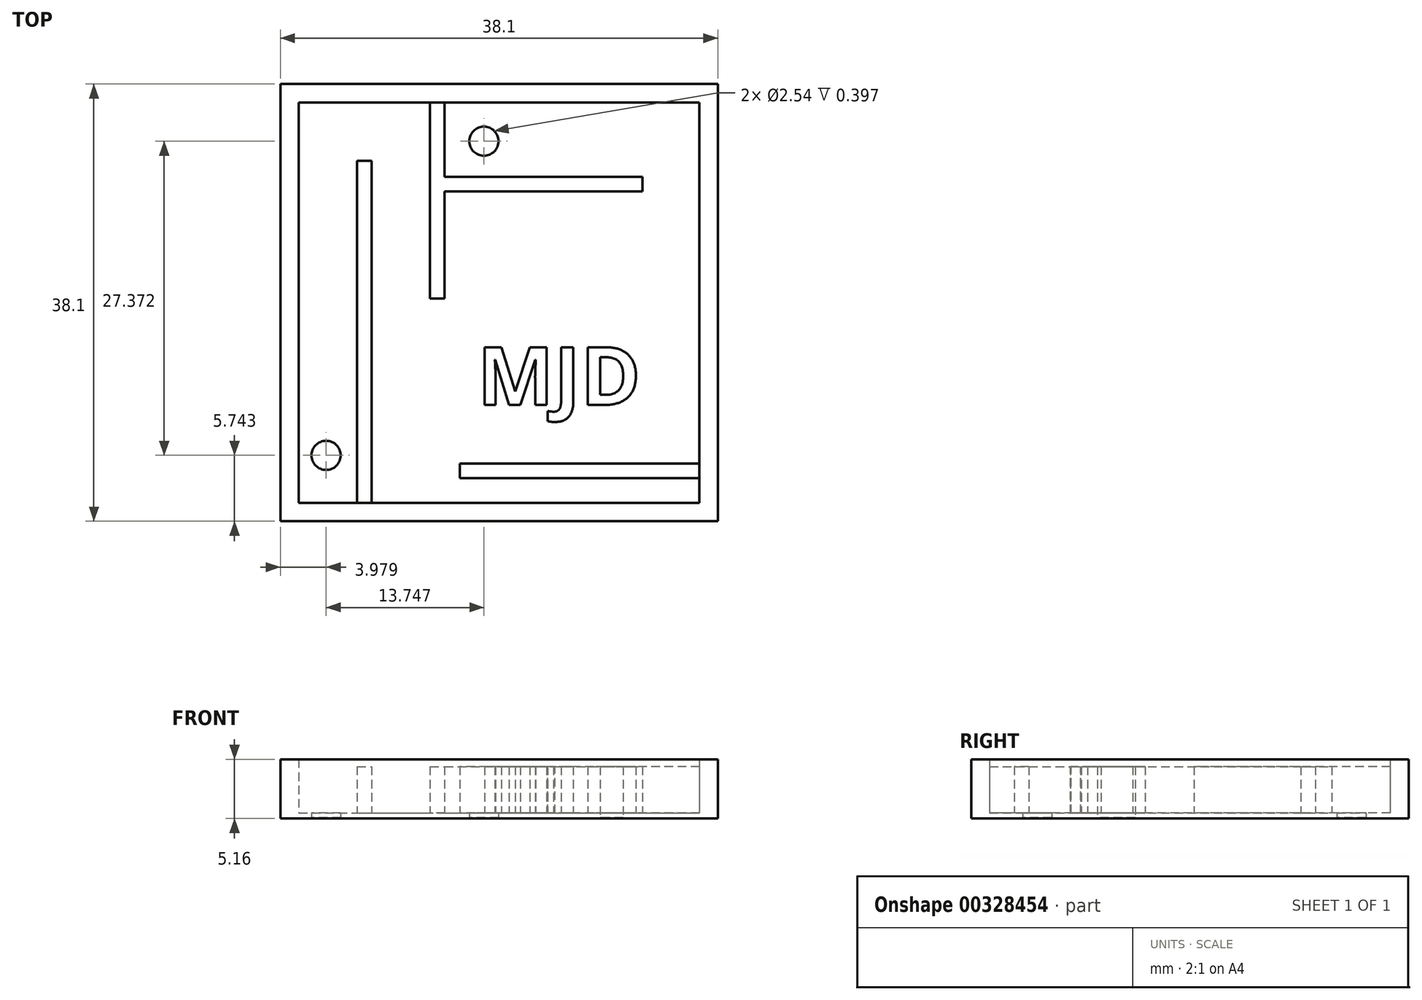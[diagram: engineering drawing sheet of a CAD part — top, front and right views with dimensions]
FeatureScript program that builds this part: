
annotation { "Feature Type Name" : "Feature", "Feature Type Description" : "" }
export const myFeature = defineFeature(function(context is Context, id is Id, definition is map)
    precondition{}
    {
        {
            var Q0;
            Q0=qCreatedBy(makeId("Top.planeOp"),FACE);
            var sketch = newSketch(context, id + "F0", { "sketchPlane" : qUnion([Q0])});
            skLineSegment(sketch, "E0.bottom", {"start": v(-22.73, 22.17) * mm, "end": v(15.37, 22.17) * mm});
            skLineSegment(sketch, "E0.top", {"start": v(-22.73, -15.93) * mm, "end": v(15.37, -15.93) * mm});
            skLineSegment(sketch, "E0.left", {"start": v(-22.73, 22.17) * mm, "end": v(-22.73, -15.93) * mm});
            skLineSegment(sketch, "E0.right", {"start": v(15.37, 22.17) * mm, "end": v(15.37, -15.93) * mm});
            skSolve(sketch);
        }
        {
            var Q0;
            Q0=makeQuery(id+"F0.imprint","IMPRINT",FACE,{"disambiguationData":[TD([[makeQuery(id+"F0.imprint","IMPRINT",EDGE,{"derivedFrom":sQuery(id+"F0.wireOp",EDGE,"E0.bottom")}),-1.0]])]});
            extrude(context, id + "F1", {"entities" : qUnion([Q0]), "depth" : 0.08 * mm});
        }
        {
            var Q0;
            Q0=makeQuery(id+"F1.opExtrude","CAP_FACE",FACE,{"disambiguationData":[OSD([sQuery(id+"F0.wireOp",EDGE,"E0.bottom"),sQuery(id+"F0.wireOp",EDGE,"E0.top"),sQuery(id+"F0.wireOp",EDGE,"E0.left"),sQuery(id+"F0.wireOp",EDGE,"E0.right")])],"isStart":false});
            var sketch = newSketch(context, id + "F2", { "sketchPlane" : qUnion([Q0])});
            skLineSegment(sketch, "E1.0", {"start": v(-21.13, 20.57) * mm, "end": v(13.77, 20.57) * mm});
            skLineSegment(sketch, "E1.1", {"start": v(-21.13, 20.57) * mm, "end": v(-21.13, -14.33) * mm});
            skLineSegment(sketch, "E1.2", {"start": v(-21.13, -14.33) * mm, "end": v(13.77, -14.33) * mm});
            skLineSegment(sketch, "E1.3", {"start": v(13.77, 20.57) * mm, "end": v(13.77, -14.33) * mm});
            skSolve(sketch);
        }
        {
            var Q0;
            Q0=makeQuery(id+"F2.imprint","IMPRINT",FACE,{"disambiguationData":[TD([[makeQuery(id+"F2.imprint","IMPRINT",EDGE,{"derivedFrom":sQuery(id+"F2.wireOp",EDGE,"E1.0")}),1.0]])]});
            extrude(context, id + "F3", {"entities" : qUnion([Q0]), "operationType" : NewBodyOperationType.ADD, "depth" : 5.08 * mm});
        }
        {
            var Q0;
            Q0=makeQuery(id+"F1.opExtrude","CAP_FACE",FACE,{"disambiguationData":[OSD([sQuery(id+"F0.wireOp",EDGE,"E0.bottom"),sQuery(id+"F0.wireOp",EDGE,"E0.top"),sQuery(id+"F0.wireOp",EDGE,"E0.left"),sQuery(id+"F0.wireOp",EDGE,"E0.right")])],"isStart":false});
            var sketch = newSketch(context, id + "F4", { "sketchPlane" : qUnion([Q0])});
            skLineSegment(sketch, "E2.bottom", {"start": v(-16.05, -14.33) * mm, "end": v(-14.78, -14.33) * mm});
            skLineSegment(sketch, "E2.top", {"start": v(-16.05, 15.49) * mm, "end": v(-14.78, 15.49) * mm});
            skLineSegment(sketch, "E2.left", {"start": v(-16.05, -14.33) * mm, "end": v(-16.05, 15.49) * mm});
            skLineSegment(sketch, "E2.right", {"start": v(-14.78, -14.33) * mm, "end": v(-14.78, 15.49) * mm});
            skLineSegment(sketch, "E3.bottom", {"start": v(-11.92, 20.57) * mm, "end": v(-9.7, 20.57) * mm});
            skLineSegment(sketch, "E4.bottom", {"start": v(13.77, -10.89) * mm, "end": v(-7.1, -10.89) * mm});
            skLineSegment(sketch, "E4.top", {"start": v(13.77, -12.16) * mm, "end": v(-7.1, -12.16) * mm});
            skLineSegment(sketch, "E4.left", {"start": v(13.77, -10.89) * mm, "end": v(13.77, -12.16) * mm});
            skLineSegment(sketch, "E4.right", {"start": v(-7.1, -10.89) * mm, "end": v(-7.1, -12.16) * mm});
            skText(sketch, "E5", { "text": "MJD", "fontName": "OpenSans-Bold.ttf"});
            skLineSegment(sketch, "E6.bottom", {"start": v(-8.43, 20.57) * mm, "end": v(-9.7, 20.57) * mm});
            skLineSegment(sketch, "E6.top", {"start": v(-8.43, 3.47) * mm, "end": v(-9.7, 3.47) * mm});
            skLineSegment(sketch, "E6.left", {"start": v(-8.43, 20.57) * mm, "end": v(-8.43, 14.07) * mm});
            skLineSegment(sketch, "E6.right", {"start": v(-9.7, 20.57) * mm, "end": v(-9.7, 3.47) * mm});
            skLineSegment(sketch, "E7.bottom", {"start": v(-8.43, 12.8) * mm, "end": v(8.8, 12.8) * mm});
            skLineSegment(sketch, "E7.top", {"start": v(-8.43, 14.07) * mm, "end": v(8.8, 14.07) * mm});
            skLineSegment(sketch, "E7.right", {"start": v(8.8, 12.8) * mm, "end": v(8.8, 14.07) * mm});
            skLineSegment(sketch, "E8.trimOffspring", {"start": v(-8.43, 12.8) * mm, "end": v(-8.43, 3.47) * mm});
            const initialGuessF4  = {"E5": [-0.00557, -0.0058, 1, 0, 0.00508]};
            skSetInitialGuess(sketch, initialGuessF4);
            skSolve(sketch);
        }
        {
            var Q0;
            Q0=makeQuery(id+"F4.imprint","IMPRINT",FACE,{"disambiguationData":[TD([[makeQuery(id+"F4.imprint","IMPRINT",EDGE,{"derivedFrom":sQuery(id+"F4.wireOp",EDGE,"E2.bottom")}),1.0]])]});
            var Q1;
            Q1=makeQuery(id+"F4.imprint","IMPRINT",FACE,{"disambiguationData":[TD([[makeQuery(id+"F4.imprint","IMPRINT",EDGE,{"derivedFrom":sQuery(id+"F4.wireOp",EDGE,"E6.bottom")}),-1.0]])]});
            var Q2;
            Q2=makeQuery(id+"F4.imprint","IMPRINT",FACE,{"disambiguationData":[TD([[makeQuery(id+"F4.imprint","IMPRINT",EDGE,{"derivedFrom":sQuery(id+"F4.wireOp",EDGE,"E4.bottom")}),1.0]])]});
            extrude(context, id + "F5", {"entities" : qUnion([Q0, Q1, Q2]), "operationType" : NewBodyOperationType.ADD, "depth" : 4.44 * mm});
        }
        {
            var Q0;
            Q0 = qSketchRegion(id + "F4", true);
            extrude(context, id + "F6", {"entities" : qUnion([Q0]), "operationType" : NewBodyOperationType.ADD, "depth" : 4.44 * mm});
        }
        {
            var Q0;
            Q0=makeQuery(id+"F4.imprint","IMPRINT",FACE,{"disambiguationData":[TD([[makeQuery(id+"F4.imprint","IMPRINT",EDGE,{"derivedFrom":sQuery(id+"F4.wireOp",EDGE,"E2.top")}),1.0]])]});
            var sketch = newSketch(context, id + "F7", { "sketchPlane" : qUnion([Q0])});
            skCircle(sketch, "E9", {"center": v(-5, 17.19) * mm, "radius": 1.27 * mm});
            skCircle(sketch, "E10", {"center": v(-18.75, -10.19) * mm, "radius": 1.27 * mm});
            skSolve(sketch);
        }
        {
            var Q0;
            Q0=makeQuery(id+"F7.imprint","IMPRINT",FACE,{"disambiguationData":[TD([[makeQuery(id+"F7.imprint","IMPRINT",EDGE,{"derivedFrom":sQuery(id+"F7.wireOp",EDGE,"E9")}),-1.0]])]});
            extrude(context, id + "F8", {"entities" : qUnion([Q0]), "operationType" : NewBodyOperationType.ADD, "depth" : 0.8 * mm});
        }
        {
            var Q0;
            Q0=makeQuery(id+"F8.opExtrude","CAP_FACE",FACE,{"disambiguationData":[OSD([sQuery(id+"F2.wireOp",EDGE,"E1.0"),sQuery(id+"F2.wireOp",EDGE,"E1.1"),sQuery(id+"F2.wireOp",EDGE,"E1.2"),sQuery(id+"F2.wireOp",EDGE,"E1.3"),sQuery(id+"F4.wireOp",EDGE,"E2.top"),sQuery(id+"F4.wireOp",EDGE,"E2.left"),sQuery(id+"F4.wireOp",EDGE,"E2.right"),sQuery(id+"F4.wireOp",EDGE,"E3.bottom"),sQuery(id+"F4.wireOp",EDGE,"E4.bottom"),sQuery(id+"F4.wireOp",EDGE,"E4.top"),sQuery(id+"F4.wireOp",EDGE,"E4.right"),sQuery(id+"F4.wireOp",EDGE,"E5.sketch_text.stroke-0"),sQuery(id+"F4.wireOp",EDGE,"E5.sketch_text.stroke-1"),sQuery(id+"F4.wireOp",EDGE,"E5.sketch_text.stroke-2"),sQuery(id+"F4.wireOp",EDGE,"E5.sketch_text.stroke-3"),sQuery(id+"F4.wireOp",EDGE,"E5.sketch_text.stroke-4"),sQuery(id+"F4.wireOp",EDGE,"E5.sketch_text.stroke-5"),sQuery(id+"F4.wireOp",EDGE,"E5.sketch_text.stroke-6"),sQuery(id+"F4.wireOp",EDGE,"E5.sketch_text.stroke-7"),sQuery(id+"F4.wireOp",EDGE,"E5.sketch_text.stroke-8"),sQuery(id+"F4.wireOp",EDGE,"E5.sketch_text.stroke-9"),sQuery(id+"F4.wireOp",EDGE,"E5.sketch_text.stroke-10"),sQuery(id+"F4.wireOp",EDGE,"E5.sketch_text.stroke-11"),sQuery(id+"F4.wireOp",EDGE,"E5.sketch_text.stroke-12"),sQuery(id+"F4.wireOp",EDGE,"E5.sketch_text.stroke-13"),sQuery(id+"F4.wireOp",EDGE,"E5.sketch_text.stroke-14"),sQuery(id+"F4.wireOp",EDGE,"E5.sketch_text.stroke-15"),sQuery(id+"F4.wireOp",EDGE,"E5.sketch_text.stroke-16"),sQuery(id+"F4.wireOp",EDGE,"E5.sketch_text.stroke-17"),sQuery(id+"F4.wireOp",EDGE,"E5.sketch_text.stroke-18"),sQuery(id+"F4.wireOp",EDGE,"E5.sketch_text.stroke-19"),sQuery(id+"F4.wireOp",EDGE,"E5.sketch_text.stroke-20"),sQuery(id+"F4.wireOp",EDGE,"E5.sketch_text.stroke-21"),sQuery(id+"F4.wireOp",EDGE,"E5.sketch_text.stroke-22"),sQuery(id+"F4.wireOp",EDGE,"E5.sketch_text.stroke-23"),sQuery(id+"F4.wireOp",EDGE,"E5.sketch_text.stroke-24"),sQuery(id+"F4.wireOp",EDGE,"E5.sketch_text.stroke-25"),sQuery(id+"F4.wireOp",EDGE,"E5.sketch_text.stroke-26"),sQuery(id+"F4.wireOp",EDGE,"E5.sketch_text.stroke-27"),sQuery(id+"F4.wireOp",EDGE,"E5.sketch_text.stroke-28"),sQuery(id+"F4.wireOp",EDGE,"E5.sketch_text.stroke-29"),sQuery(id+"F4.wireOp",EDGE,"E5.sketch_text.stroke-30"),sQuery(id+"F4.wireOp",EDGE,"E5.sketch_text.stroke-31"),sQuery(id+"F4.wireOp",EDGE,"E5.sketch_text.stroke-32"),sQuery(id+"F4.wireOp",EDGE,"E5.sketch_text.stroke-33"),sQuery(id+"F4.wireOp",EDGE,"E5.sketch_text.stroke-34"),sQuery(id+"F4.wireOp",EDGE,"E5.sketch_text.stroke-35"),sQuery(id+"F4.wireOp",EDGE,"E6.top"),sQuery(id+"F4.wireOp",EDGE,"E6.left"),sQuery(id+"F4.wireOp",EDGE,"E6.right"),sQuery(id+"F4.wireOp",EDGE,"E7.bottom"),sQuery(id+"F4.wireOp",EDGE,"E7.top"),sQuery(id+"F4.wireOp",EDGE,"E7.right"),sQuery(id+"F4.wireOp",EDGE,"E8.trimOffspring"),sQuery(id+"F7.wireOp",EDGE,"E9"),sQuery(id+"F7.wireOp",EDGE,"E10")])],"isStart":false});
            extrude(context, id + "F9", {"entities" : qUnion([Q0]), "operationType" : NewBodyOperationType.REMOVE, "oppositeDirection" : true, "depth" : 0.4 * mm});
        }
    });
